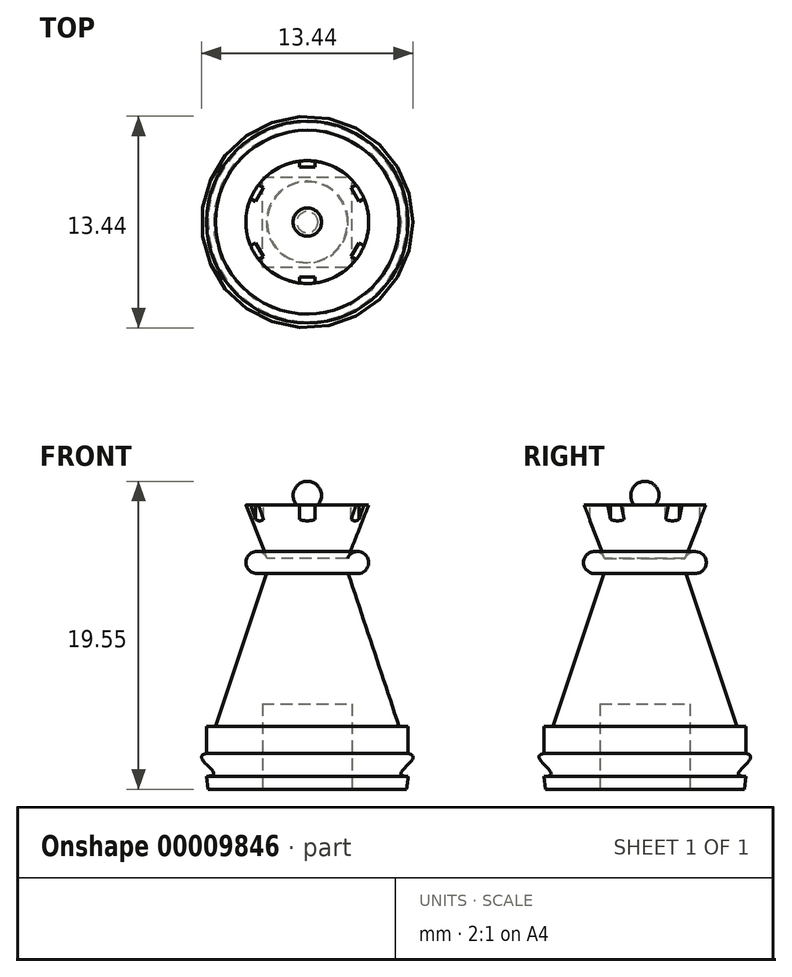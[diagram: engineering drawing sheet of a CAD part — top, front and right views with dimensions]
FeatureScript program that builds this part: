
annotation { "Feature Type Name" : "Feature", "Feature Type Description" : "" }
export const myFeature = defineFeature(function(context is Context, id is Id, definition is map)
    precondition{}
    {
        {
            var Q0;
            Q0=qCreatedBy(makeId("Front.planeOp"),FACE);
            var sketch = newSketch(context, id + "F0", { "sketchPlane" : qUnion([Q0])});
            skLineSegment(sketch, "E0", {"start": v(-2.6, 5.72) * mm, "end": v(-5.83, -4) * mm});
            skLineSegment(sketch, "E1", {"start": v(0, 11.57) * mm, "end": v(0, -10.5) * mm, "construction": true});
            skLineSegment(sketch, "E2.bottom", {"start": v(-2.6, 5.72) * mm, "end": v(-3.9, 5.72) * mm});
            skLineSegment(sketch, "E2.top", {"start": v(-0.67, 10.07) * mm, "end": v(-3.9, 10.07) * mm});
            skLineSegment(sketch, "E2.right", {"start": v(-3.9, 5.72) * mm, "end": v(-3.9, 10.07) * mm, "construction": true});
            skLineSegment(sketch, "E3", {"start": v(-6.31, -7.98) * mm, "end": v(0, -7.98) * mm});
            skFitSpline(sketch, "E4", {"points": [v(-6.4, -5.72) * mm, v(-6.69, -5.85) * mm, v(-6.4, -7.16) * mm], "startDerivative": vector(4.53, 1) * mm, "endDerivative": vector(-5.78, 0) * mm});
            skLineSegment(sketch, "E5", {"start": v(-6.4, -7.16) * mm, "end": v(-6.31, -7.98) * mm});
            skLineSegment(sketch, "E6", {"start": v(-6.4, -5.72) * mm, "end": v(-6.4, -4) * mm});
            skLineSegment(sketch, "E7", {"start": v(-6.4, -4) * mm, "end": v(-5.83, -4) * mm});
            skArc(sketch, "E8", {"start": v(0, 11.57) * mm, "mid": v(-0.82, 11.04) * mm, "end": v(-0.67, 10.07) * mm});
            skLineSegment(sketch, "E9", {"start": v(0, 11.57) * mm, "end": v(0, -7.98) * mm});
            skArc(sketch, "E10", {"start": v(-2.55, 6.68) * mm, "mid": v(-3.78, 6.81) * mm, "end": v(-3.2, 5.72) * mm});
            skLineSegment(sketch, "E11", {"start": v(-3.9, 10.07) * mm, "end": v(-2.55, 6.68) * mm});
            skSolve(sketch);
        }
        {
            var Q0;
            Q0 = qSketchRegion(id + "F0", true);
            var Q1;
            Q1=sQuery(id+"F0.wireOp",EDGE,"E9");
            revolve(context, id + "F1", {"entities" : qUnion([Q0]), "axis" : qUnion([Q1]), "revolveType" : RevolveType.FULL});
        }
        {
            var Q0;
            Q0=makeQuery(id+"F1.opRevolve","SWEPT_FACE",FACE,{"disambiguationData":[OSD([sQuery(id+"F0.wireOp",EDGE,"E2.top")])]});
            var sketch = newSketch(context, id + "F2", { "sketchPlane" : qUnion([Q0])});
            skLineSegment(sketch, "E12.bottom", {"start": v(-0.5, 3.9) * mm, "end": v(0.5, 3.9) * mm});
            skLineSegment(sketch, "E12.top", {"start": v(-0.5, 3.5) * mm, "end": v(0.5, 3.5) * mm});
            skLineSegment(sketch, "E12.left", {"start": v(-0.5, 3.9) * mm, "end": v(-0.5, 3.5) * mm});
            skLineSegment(sketch, "E12.right", {"start": v(0.5, 3.9) * mm, "end": v(0.5, 3.5) * mm});
            skPoint(sketch, "E13", {"position": v(0, 3.5) * mm});
            skLineSegment(sketch, "E14", {"start": v(0, 5.34) * mm, "end": v(0, 1.46) * mm, "construction": true});
            skLineSegment(sketch, "E15.1.0", {"start": v(-3.28, 1.32) * mm, "end": v(-2.78, 2.18) * mm});
            skLineSegment(sketch, "E15.1.1", {"start": v(-3.13, 2.38) * mm, "end": v(-2.78, 2.18) * mm});
            skLineSegment(sketch, "E15.1.2", {"start": v(-3.63, 1.52) * mm, "end": v(-3.13, 2.38) * mm});
            skLineSegment(sketch, "E15.1.3", {"start": v(-3.63, 1.52) * mm, "end": v(-3.28, 1.32) * mm});
            skLineSegment(sketch, "E15.2.0", {"start": v(-2.78, -2.18) * mm, "end": v(-3.28, -1.32) * mm});
            skLineSegment(sketch, "E15.2.1", {"start": v(-3.63, -1.52) * mm, "end": v(-3.28, -1.32) * mm});
            skLineSegment(sketch, "E15.2.2", {"start": v(-3.13, -2.38) * mm, "end": v(-3.63, -1.52) * mm});
            skLineSegment(sketch, "E15.2.3", {"start": v(-3.13, -2.38) * mm, "end": v(-2.78, -2.18) * mm});
            skLineSegment(sketch, "E15.3.0", {"start": v(0.5, -3.5) * mm, "end": v(-0.5, -3.5) * mm});
            skLineSegment(sketch, "E15.3.1", {"start": v(-0.5, -3.9) * mm, "end": v(-0.5, -3.5) * mm});
            skLineSegment(sketch, "E15.3.2", {"start": v(0.5, -3.9) * mm, "end": v(-0.5, -3.9) * mm});
            skLineSegment(sketch, "E15.3.3", {"start": v(0.5, -3.9) * mm, "end": v(0.5, -3.5) * mm});
            skLineSegment(sketch, "E15.4.0", {"start": v(3.28, -1.32) * mm, "end": v(2.78, -2.18) * mm});
            skLineSegment(sketch, "E15.4.1", {"start": v(3.13, -2.38) * mm, "end": v(2.78, -2.18) * mm});
            skLineSegment(sketch, "E15.4.2", {"start": v(3.63, -1.52) * mm, "end": v(3.13, -2.38) * mm});
            skLineSegment(sketch, "E15.4.3", {"start": v(3.63, -1.52) * mm, "end": v(3.28, -1.32) * mm});
            skLineSegment(sketch, "E15.5.0", {"start": v(2.78, 2.18) * mm, "end": v(3.28, 1.32) * mm});
            skLineSegment(sketch, "E15.5.1", {"start": v(3.63, 1.52) * mm, "end": v(3.28, 1.32) * mm});
            skLineSegment(sketch, "E15.5.2", {"start": v(3.13, 2.38) * mm, "end": v(3.63, 1.52) * mm});
            skLineSegment(sketch, "E15.5.3", {"start": v(3.13, 2.38) * mm, "end": v(2.78, 2.18) * mm});
            skPoint(sketch, "E15.center", {"position": v(0, 0) * mm});
            skSolve(sketch);
        }
        {
            var Q0;
            Q0 = qSketchRegion(id + "F2", true);
            extrude(context, id + "F3", {"entities" : qUnion([Q0]), "operationType" : NewBodyOperationType.REMOVE, "oppositeDirection" : true, "depth" : 2 * mm});
        }
        {
            var Q0;
            Q0=makeQuery(id+"F1.opRevolve","SWEPT_FACE",FACE,{"disambiguationData":[OSD([sQuery(id+"F0.wireOp",EDGE,"E3")])]});
            var sketch = newSketch(context, id + "F4", { "sketchPlane" : qUnion([Q0])});
            skLineSegment(sketch, "E16.bottom", {"start": v(-2.85, 2.85) * mm, "end": v(2.85, 2.85) * mm});
            skLineSegment(sketch, "E16.top", {"start": v(-2.85, -2.85) * mm, "end": v(2.85, -2.85) * mm});
            skLineSegment(sketch, "E16.left", {"start": v(-2.85, 2.85) * mm, "end": v(-2.85, -2.85) * mm});
            skLineSegment(sketch, "E16.right", {"start": v(2.85, 2.85) * mm, "end": v(2.85, -2.85) * mm});
            skLineSegment(sketch, "E17", {"start": v(0, 2.85) * mm, "end": v(0, -2.85) * mm, "construction": true});
            skPoint(sketch, "E18", {"position": v(0, 0) * mm});
            skSolve(sketch);
        }
        {
            var Q0;
            Q0 = qSketchRegion(id + "F4", true);
            extrude(context, id + "F5", {"entities" : qUnion([Q0]), "operationType" : NewBodyOperationType.REMOVE, "oppositeDirection" : true, "depth" : 5.4 * mm});
        }
    });
